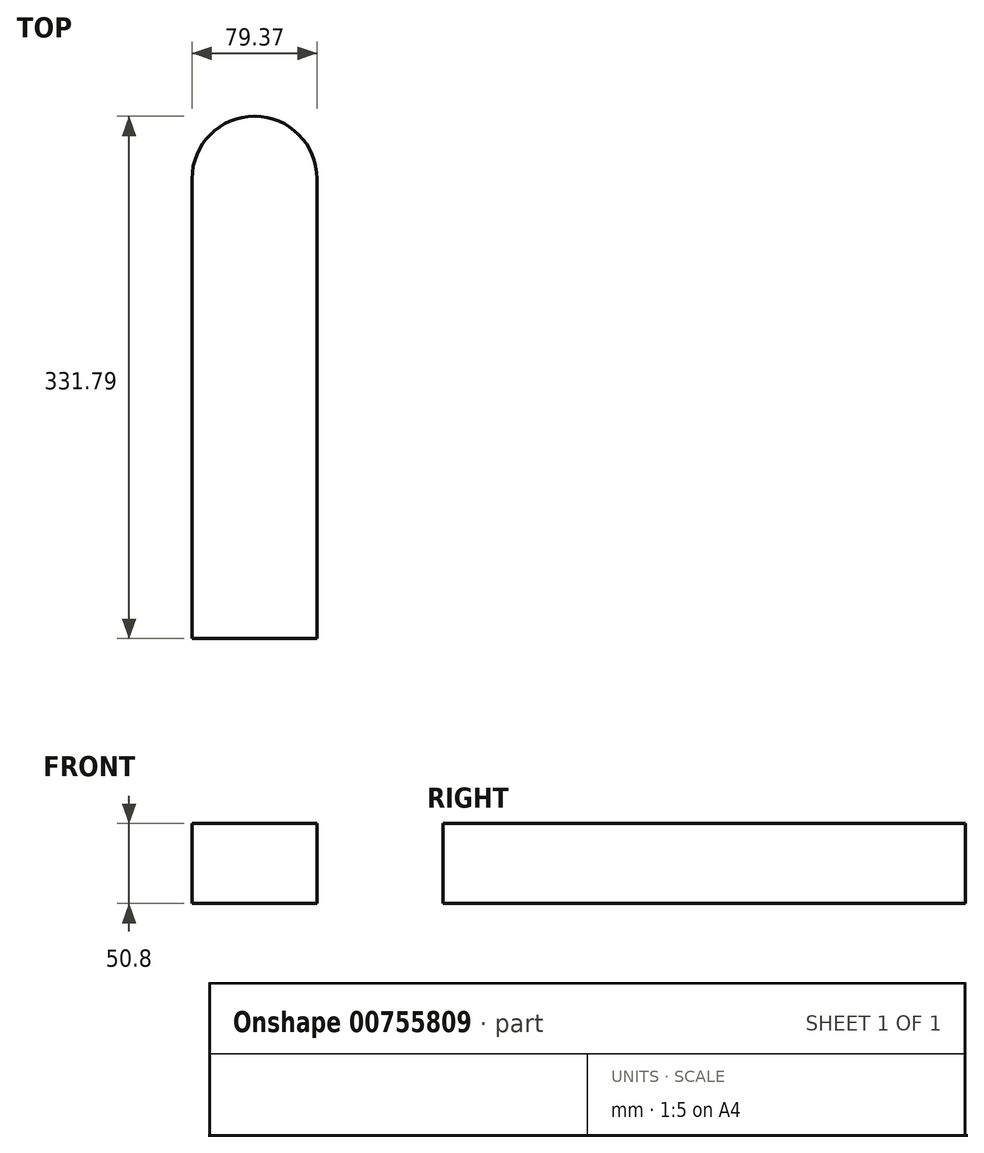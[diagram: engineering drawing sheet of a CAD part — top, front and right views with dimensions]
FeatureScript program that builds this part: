
annotation { "Feature Type Name" : "Feature", "Feature Type Description" : "" }
export const myFeature = defineFeature(function(context is Context, id is Id, definition is map)
    precondition{}
    {
        {
            var Q0;
            Q0=qCreatedBy(makeId("Top.planeOp"),FACE);
            var sketch = newSketch(context, id + "F0", { "sketchPlane" : qUnion([Q0])});
            skLineSegment(sketch, "E0.top", {"start": v(-55.2, -209.57) * mm, "end": v(24.18, -209.57) * mm});
            skLineSegment(sketch, "E0.left", {"start": v(-55.2, 82.53) * mm, "end": v(-55.2, -209.57) * mm});
            skLineSegment(sketch, "E0.right", {"start": v(24.18, 82.53) * mm, "end": v(24.18, -209.57) * mm});
            skArc(sketch, "E1", {"start": v(24.18, 82.53) * mm, "mid": v(-15.5, 122.22) * mm, "end": v(-55.2, 82.53) * mm});
            skSolve(sketch);
        }
        {
            var Q0;
            Q0=qSketchRegion(id+"F0",true);
            extrude(context, id + "F1", {"entities" : qUnion([Q0]), "depth" : 50.8 * mm, "offsetDistance" : 25.4 * mm});
        }
    });
